# Revit family: ARKOSLIGHT_Micro Shaper 24V 52
name_source: partatom
category: Lighting Fixtures
units: mm (PartAtom-declared; Revit-internal decimal feet)

## family parameters
Cut with Voids When Loaded = No
Host = Face
Light Source = No
Part Type = Normal
Room Calculation Point = No
Round Connector Dimension = Use Diameter
Shared = No

## types (3) — shared parameters
ARKOSLIGHT_Apparent Load = 2 VA
ARKOSLIGHT_Beam Angle = 52.00°
ARKOSLIGHT_Body Color = ARKOSLIGHT_Black
ARKOSLIGHT_CRI = CRI>90
ARKOSLIGHT_Color = Black
ARKOSLIGHT_Dimming = DIM options
ARKOSLIGHT_Efficiency = 29%
ARKOSLIGHT_Fixture Type = TRACKLIGHTS
ARKOSLIGHT_IP = 20
ARKOSLIGHT_Model = MICRO SHAPER 24V
ARKOSLIGHT_Series = MICRO SHAPER 24V
ARKOSLIGHT_Wattage = 3 W
Apparent Load = 2 VA
Manufacturer = ARKOSLIGHT
Model = MICRO SHAPER 24V
URL = https://www.arkoslight.com
zero-valued in all types: Default Elevation

## per-type parameters (varying)
| type | ARKOSLIGHT_CCT | ARKOSLIGHT_IES | ARKOSLIGHT_Luminous flux | ARKOSLIGHT_Reference | IES |
| A5440010N - MICRO SHAPER 24V 52º 2700K N | 2700 K | A544-00-10 MICRO SHAPER 24V 52 2700K CRI90.ies | 190 lm | A5440010N | IES : A5440010N - MICRO SHAPER 24V 52º 2700K N |
| A5440011N - MICRO SHAPER 24V 52º 3000K N | 3000 K | A544-00-11 MICRO SHAPER 24V 52 3000K CRI90.ies | 210 lm | A5440011N | IES : A5440011N - MICRO SHAPER 24V 52º 3000K N |
| A5440012N - MICRO SHAPER 24V 52º 4000K N | 4000 K | A544-00-12 MICRO SHAPER 24V 52 4000K CRI90.ies | 250 lm | A5440012N | IES : A5440012N - MICRO SHAPER 24V 52º 4000K N |

## geometry (parser evidence)
native form markers: Sweep x18
no freeform markers — native parametric forms only
